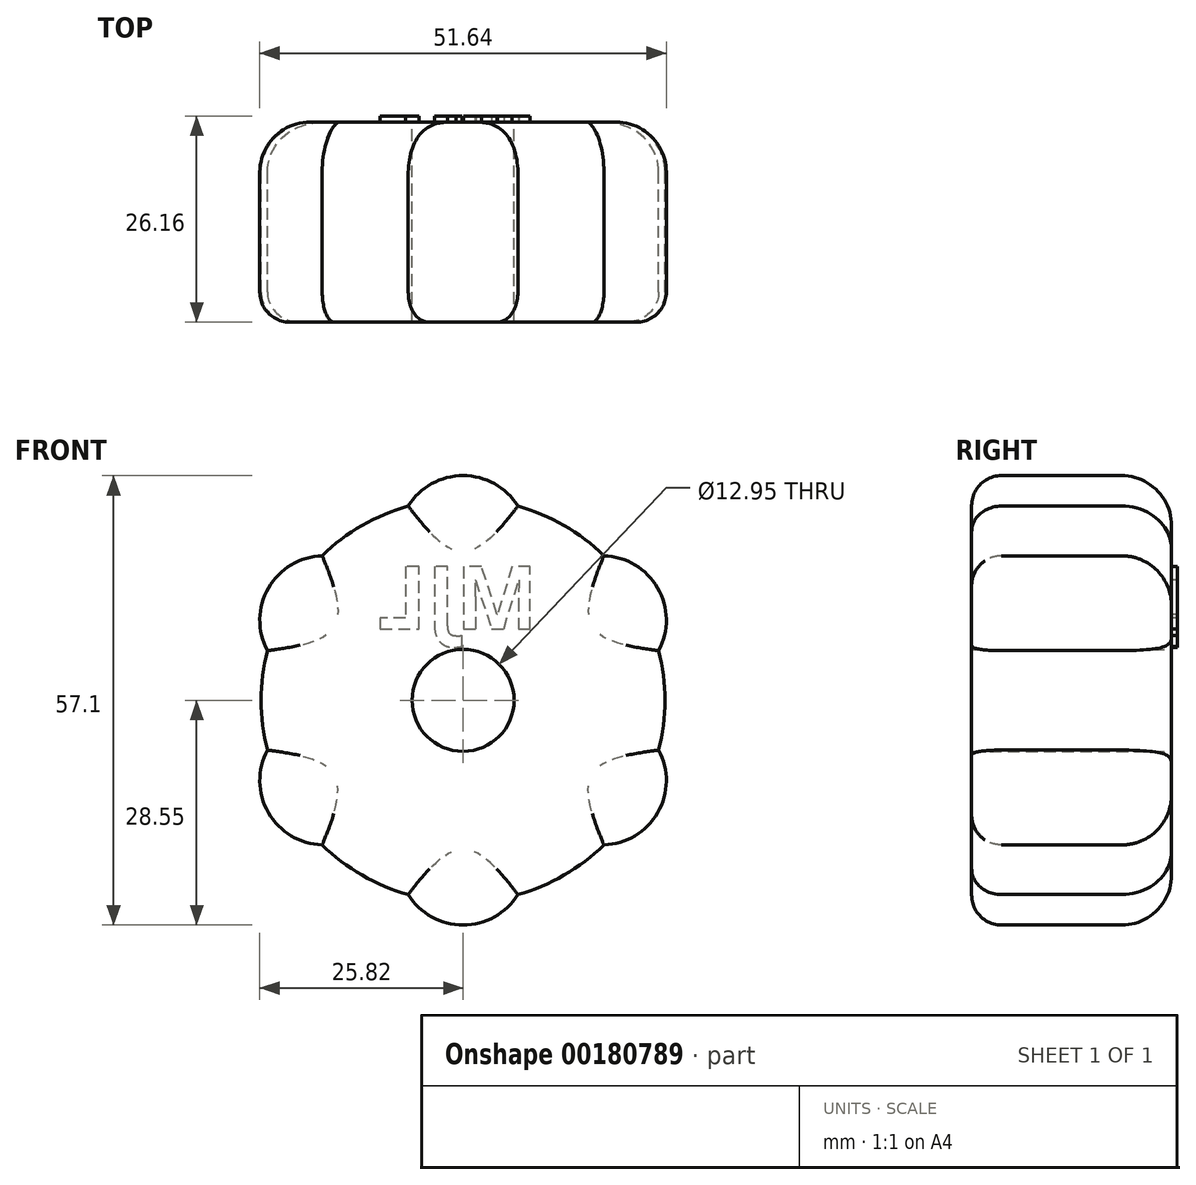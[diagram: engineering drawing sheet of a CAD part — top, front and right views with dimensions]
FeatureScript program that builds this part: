
annotation { "Feature Type Name" : "Feature", "Feature Type Description" : "" }
export const myFeature = defineFeature(function(context is Context, id is Id, definition is map)
    precondition{}
    {
        {
            var Q0;
            Q0=qCreatedBy(makeId("Front.planeOp"),FACE);
            var sketch = newSketch(context, id + "F0", { "sketchPlane" : qUnion([Q0])});
            skCircle(sketch, "E0", {"center": v(0, 0) * mm, "radius": 6.48 * mm});
            skArc(sketch, "E1", {"start": v(-6.96, 24.68) * mm, "mid": v(-12.82, 22.2) * mm, "end": v(-17.9, 18.37) * mm});
            skArc(sketch, "E2", {"start": v(6.96, 24.68) * mm, "mid": v(0, 28.55) * mm, "end": v(-6.96, 24.68) * mm});
            skArc(sketch, "E3.1.0", {"start": v(-17.9, 18.37) * mm, "mid": v(-24.72, 14.27) * mm, "end": v(-24.85, 6.31) * mm});
            skArc(sketch, "E3.2.0", {"start": v(-24.85, -6.31) * mm, "mid": v(-24.72, -14.27) * mm, "end": v(-17.9, -18.37) * mm});
            skArc(sketch, "E3.3.0", {"start": v(-6.96, -24.68) * mm, "mid": v(0, -28.55) * mm, "end": v(6.96, -24.68) * mm});
            skArc(sketch, "E3.4.0", {"start": v(17.9, -18.37) * mm, "mid": v(24.72, -14.27) * mm, "end": v(24.85, -6.31) * mm});
            skArc(sketch, "E3.5.0", {"start": v(24.85, 6.31) * mm, "mid": v(24.72, 14.27) * mm, "end": v(17.9, 18.37) * mm});
            skArc(sketch, "E4.trimOffspring", {"start": v(-24.85, 6.31) * mm, "mid": v(-25.64, 0) * mm, "end": v(-24.85, -6.31) * mm});
            skArc(sketch, "E5.trimOffspring", {"start": v(-17.9, -18.37) * mm, "mid": v(-12.82, -22.2) * mm, "end": v(-6.96, -24.68) * mm});
            skArc(sketch, "E6.trimOffspring", {"start": v(6.96, -24.68) * mm, "mid": v(12.82, -22.2) * mm, "end": v(17.9, -18.37) * mm});
            skArc(sketch, "E7.trimOffspring", {"start": v(24.85, -6.31) * mm, "mid": v(25.64, 0) * mm, "end": v(24.85, 6.31) * mm});
            skArc(sketch, "E8.trimOffspring", {"start": v(17.9, 18.37) * mm, "mid": v(12.82, 22.2) * mm, "end": v(6.96, 24.68) * mm});
            skSolve(sketch);
        }
        {
            var Q0;
            Q0=makeQuery(id+"F0.imprint","IMPRINT",FACE,{"disambiguationData":[TD([[makeQuery(id+"F0.imprint","IMPRINT",EDGE,{"derivedFrom":sQuery(id+"F0.wireOp",EDGE,"E0")}),-1.0]])]});
            extrude(context, id + "F1", {"entities" : qUnion([Q0]), "depth" : 25.4 * mm});
        }
        {
            var Q0;
            Q0=makeQuery(id+"F1.opExtrude","CAP_EDGE",EDGE,{"disambiguationData":[OSD([sQuery(id+"F0.wireOp",EDGE,"E4.trimOffspring")])],"isStart":false});
            var Q1;
            Q1=makeQuery(id+"F1.opExtrude","CAP_EDGE",EDGE,{"disambiguationData":[OSD([sQuery(id+"F0.wireOp",EDGE,"E3.2.0")])],"isStart":false});
            var Q2;
            Q2=makeQuery(id+"F1.opExtrude","CAP_EDGE",EDGE,{"disambiguationData":[OSD([sQuery(id+"F0.wireOp",EDGE,"E5.trimOffspring")])],"isStart":false});
            var Q3;
            Q3=makeQuery(id+"F1.opExtrude","CAP_EDGE",EDGE,{"disambiguationData":[OSD([sQuery(id+"F0.wireOp",EDGE,"E3.1.0")])],"isStart":false});
            var Q4;
            Q4=makeQuery(id+"F1.opExtrude","CAP_EDGE",EDGE,{"disambiguationData":[OSD([sQuery(id+"F0.wireOp",EDGE,"E1")])],"isStart":false});
            var Q5;
            Q5=makeQuery(id+"F1.opExtrude","CAP_EDGE",EDGE,{"disambiguationData":[OSD([sQuery(id+"F0.wireOp",EDGE,"E2")])],"isStart":false});
            var Q6;
            Q6=makeQuery(id+"F1.opExtrude","CAP_EDGE",EDGE,{"disambiguationData":[OSD([sQuery(id+"F0.wireOp",EDGE,"E8.trimOffspring")])],"isStart":false});
            var Q7;
            Q7=makeQuery(id+"F1.opExtrude","CAP_EDGE",EDGE,{"disambiguationData":[OSD([sQuery(id+"F0.wireOp",EDGE,"E3.5.0")])],"isStart":false});
            var Q8;
            Q8=makeQuery(id+"F1.opExtrude","CAP_EDGE",EDGE,{"disambiguationData":[OSD([sQuery(id+"F0.wireOp",EDGE,"E7.trimOffspring")])],"isStart":false});
            var Q9;
            Q9=makeQuery(id+"F1.opExtrude","CAP_EDGE",EDGE,{"disambiguationData":[OSD([sQuery(id+"F0.wireOp",EDGE,"E3.4.0")])],"isStart":false});
            var Q10;
            Q10=makeQuery(id+"F1.opExtrude","CAP_EDGE",EDGE,{"disambiguationData":[OSD([sQuery(id+"F0.wireOp",EDGE,"E6.trimOffspring")])],"isStart":false});
            var Q11;
            Q11=makeQuery(id+"F1.opExtrude","CAP_EDGE",EDGE,{"disambiguationData":[OSD([sQuery(id+"F0.wireOp",EDGE,"E3.3.0")])],"isStart":false});
            fillet(context, id + "F2", {"entities" : qUnion([Q0, Q1, Q2, Q3, Q4, Q5, Q6, Q7, Q8, Q9, Q10, Q11]), "radius" : 3.8 * mm, "tangentPropagation" : true, "allowEdgeOverflow" : false});
        }
        {
            var Q0;
            Q0=makeQuery(id+"F1.opExtrude","CAP_EDGE",EDGE,{"disambiguationData":[OSD([sQuery(id+"F0.wireOp",EDGE,"E1")])],"isStart":true});
            var Q1;
            Q1=makeQuery(id+"F1.opExtrude","CAP_EDGE",EDGE,{"disambiguationData":[OSD([sQuery(id+"F0.wireOp",EDGE,"E2")])],"isStart":true});
            var Q2;
            Q2=makeQuery(id+"F1.opExtrude","CAP_EDGE",EDGE,{"disambiguationData":[OSD([sQuery(id+"F0.wireOp",EDGE,"E8.trimOffspring")])],"isStart":true});
            var Q3;
            Q3=makeQuery(id+"F1.opExtrude","CAP_EDGE",EDGE,{"disambiguationData":[OSD([sQuery(id+"F0.wireOp",EDGE,"E3.5.0")])],"isStart":true});
            var Q4;
            Q4=makeQuery(id+"F1.opExtrude","CAP_EDGE",EDGE,{"disambiguationData":[OSD([sQuery(id+"F0.wireOp",EDGE,"E7.trimOffspring")])],"isStart":true});
            var Q5;
            Q5=makeQuery(id+"F1.opExtrude","CAP_EDGE",EDGE,{"disambiguationData":[OSD([sQuery(id+"F0.wireOp",EDGE,"E3.4.0")])],"isStart":true});
            var Q6;
            Q6=makeQuery(id+"F1.opExtrude","CAP_EDGE",EDGE,{"disambiguationData":[OSD([sQuery(id+"F0.wireOp",EDGE,"E6.trimOffspring")])],"isStart":true});
            var Q7;
            Q7=makeQuery(id+"F1.opExtrude","CAP_EDGE",EDGE,{"disambiguationData":[OSD([sQuery(id+"F0.wireOp",EDGE,"E3.3.0")])],"isStart":true});
            var Q8;
            Q8=makeQuery(id+"F1.opExtrude","CAP_EDGE",EDGE,{"disambiguationData":[OSD([sQuery(id+"F0.wireOp",EDGE,"E5.trimOffspring")])],"isStart":true});
            var Q9;
            Q9=makeQuery(id+"F1.opExtrude","CAP_EDGE",EDGE,{"disambiguationData":[OSD([sQuery(id+"F0.wireOp",EDGE,"E3.2.0")])],"isStart":true});
            var Q10;
            Q10=makeQuery(id+"F1.opExtrude","CAP_EDGE",EDGE,{"disambiguationData":[OSD([sQuery(id+"F0.wireOp",EDGE,"E4.trimOffspring")])],"isStart":true});
            var Q11;
            Q11=makeQuery(id+"F1.opExtrude","CAP_EDGE",EDGE,{"disambiguationData":[OSD([sQuery(id+"F0.wireOp",EDGE,"E3.1.0")])],"isStart":true});
            fillet(context, id + "F3", {"entities" : qUnion([Q0, Q1, Q2, Q3, Q4, Q5, Q6, Q7, Q8, Q9, Q10, Q11]), "radius" : 6.35 * mm, "tangentPropagation" : true, "allowEdgeOverflow" : false});
        }
        {
            var Q0;
            Q0=makeQuery(id+"F1.opExtrude","CAP_FACE",FACE,{"disambiguationData":[OSD([sQuery(id+"F0.wireOp",EDGE,"E0"),sQuery(id+"F0.wireOp",EDGE,"E1"),sQuery(id+"F0.wireOp",EDGE,"E2"),sQuery(id+"F0.wireOp",EDGE,"E3.1.0"),sQuery(id+"F0.wireOp",EDGE,"E3.2.0"),sQuery(id+"F0.wireOp",EDGE,"E3.3.0"),sQuery(id+"F0.wireOp",EDGE,"E3.4.0"),sQuery(id+"F0.wireOp",EDGE,"E3.5.0"),sQuery(id+"F0.wireOp",EDGE,"E4.trimOffspring"),sQuery(id+"F0.wireOp",EDGE,"E5.trimOffspring"),sQuery(id+"F0.wireOp",EDGE,"E6.trimOffspring"),sQuery(id+"F0.wireOp",EDGE,"E7.trimOffspring"),sQuery(id+"F0.wireOp",EDGE,"E8.trimOffspring")])],"isStart":true});
            var sketch = newSketch(context, id + "F4", { "sketchPlane" : qUnion([Q0])});
            skText(sketch, "E9", { "text": "MJL", "fontName": "OpenSans-Bold.ttf"});
            const initialGuessF4  = {"E9": [-0.00953, 0.00907, 1, 0, 0.008]};
            skSetInitialGuess(sketch, initialGuessF4);
            skSolve(sketch);
        }
        {
            var Q0;
            Q0 = qSketchRegion(id + "F4", true);
            extrude(context, id + "F5", {"entities" : qUnion([Q0]), "operationType" : NewBodyOperationType.ADD, "depth" : 0.76 * mm});
        }
    });
